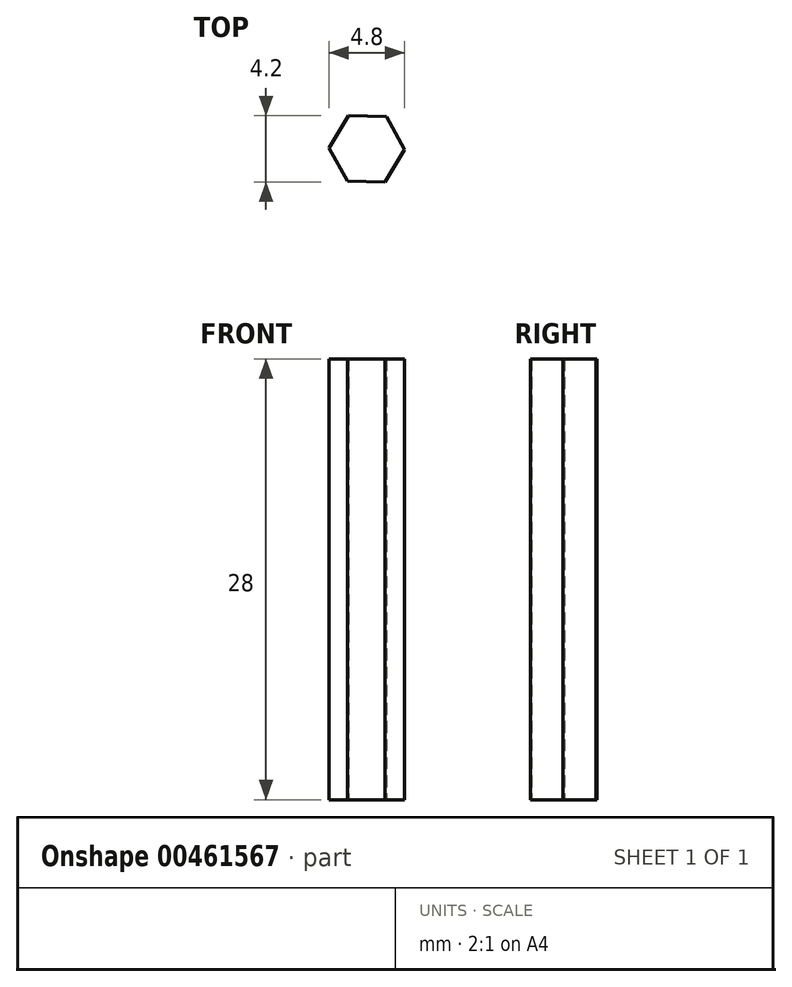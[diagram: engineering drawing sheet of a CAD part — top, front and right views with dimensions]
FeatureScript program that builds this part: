
annotation { "Feature Type Name" : "Feature", "Feature Type Description" : "" }
export const myFeature = defineFeature(function(context is Context, id is Id, definition is map)
    precondition{}
    {
        {
            var Q0;
            Q0=qCreatedBy(makeId("Top.planeOp"),FACE);
            var sketch = newSketch(context, id + "F0", { "sketchPlane" : qUnion([Q0])});
            skCircle(sketch, "E0.cCircle", {"center": v(-52.19, 29.07) * mm, "radius": 2.08 * mm, "construction": true});
            skLineSegment(sketch, "E0.0", {"start": v(-49.79, 29.02) * mm, "end": v(-51.03, 26.97) * mm});
            skLineSegment(sketch, "E0.1", {"start": v(-51.03, 26.97) * mm, "end": v(-53.43, 27.02) * mm});
            skLineSegment(sketch, "E0.2", {"start": v(-53.43, 27.02) * mm, "end": v(-54.59, 29.12) * mm});
            skLineSegment(sketch, "E0.3", {"start": v(-54.59, 29.12) * mm, "end": v(-53.34, 31.17) * mm});
            skLineSegment(sketch, "E0.4", {"start": v(-53.34, 31.17) * mm, "end": v(-50.94, 31.12) * mm});
            skLineSegment(sketch, "E0.5", {"start": v(-50.94, 31.12) * mm, "end": v(-49.79, 29.02) * mm});
            skPoint(sketch, "E0.0.midPoint", {"position": v(-50.4, 28) * mm});
            skSolve(sketch);
        }
        {
            var Q0;
            Q0 = qSketchRegion(id + "F0", true);
            extrude(context, id + "F1", {"entities" : qUnion([Q0]), "depth" : 28 * mm});
        }
    });
